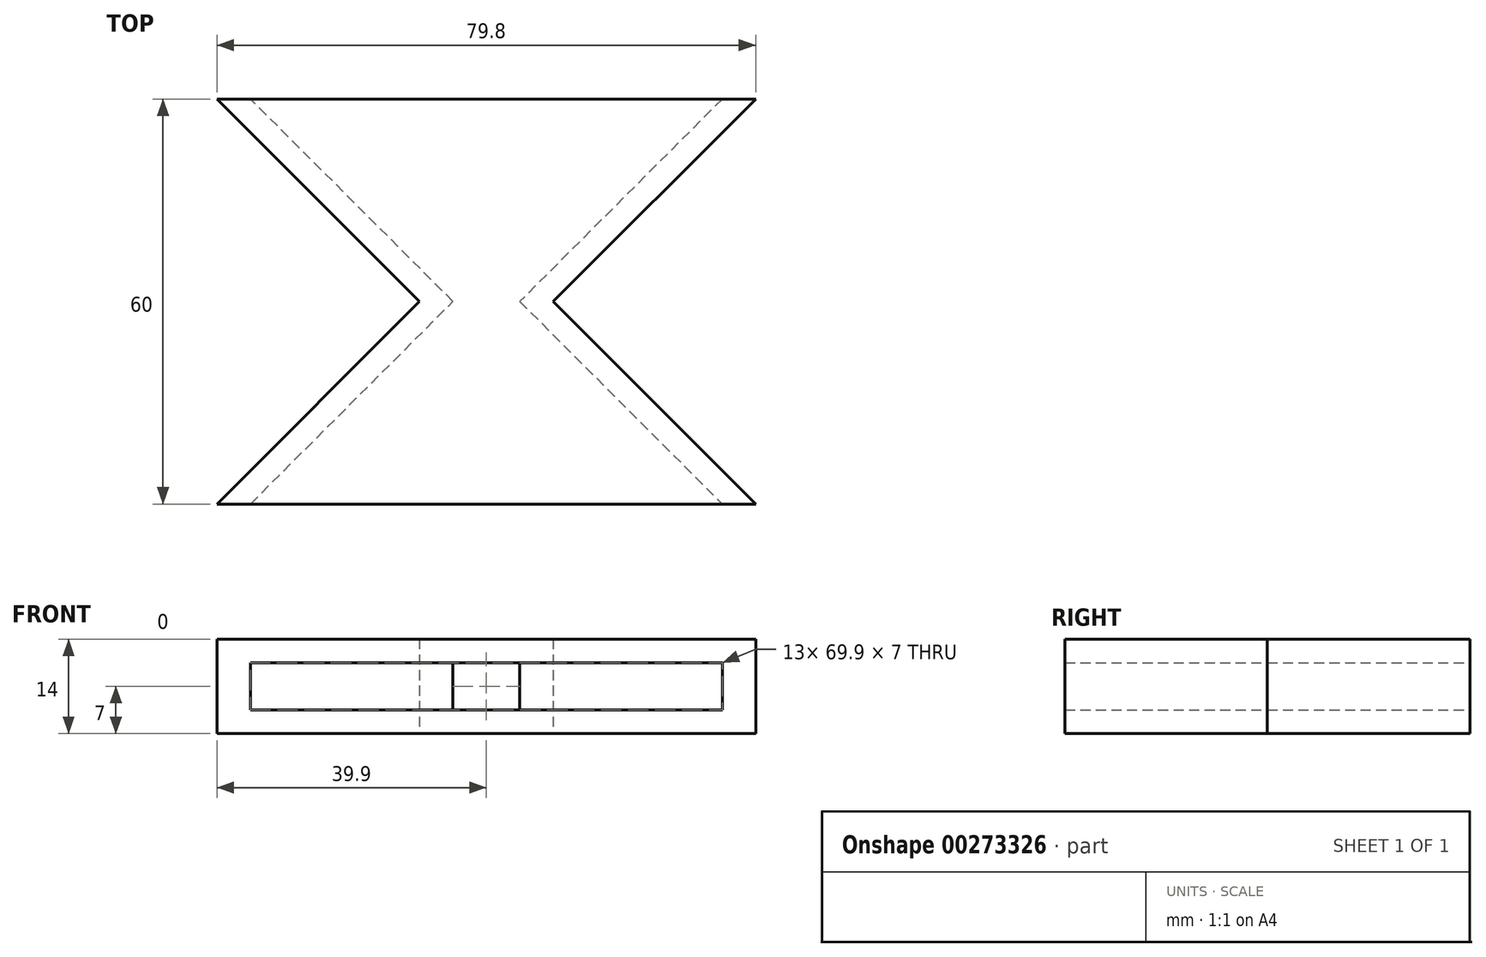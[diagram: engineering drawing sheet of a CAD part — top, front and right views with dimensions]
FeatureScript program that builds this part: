
annotation { "Feature Type Name" : "Feature", "Feature Type Description" : "" }
export const myFeature = defineFeature(function(context is Context, id is Id, definition is map)
    precondition{}
    {
        {
            var Q0;
            Q0=qCreatedBy(makeId("Top.planeOp"),FACE);
            var sketch = newSketch(context, id + "F0", { "sketchPlane" : qUnion([Q0])});
            skLineSegment(sketch, "E0", {"start": v(-39.9, 30) * mm, "end": v(39.9, 30) * mm});
            skLineSegment(sketch, "E1", {"start": v(39.9, 30) * mm, "end": v(9.9, 0) * mm});
            skLineSegment(sketch, "E2", {"start": v(9.9, 0) * mm, "end": v(39.9, -30) * mm});
            skLineSegment(sketch, "E3", {"start": v(39.9, -30) * mm, "end": v(-39.9, -30) * mm});
            skLineSegment(sketch, "E4", {"start": v(-39.9, -30) * mm, "end": v(-9.9, 0) * mm});
            skLineSegment(sketch, "E5", {"start": v(-9.9, 0) * mm, "end": v(-39.9, 30) * mm});
            skSolve(sketch);
        }
        {
            var Q0;
            Q0=makeQuery(id+"F0.imprint","IMPRINT",FACE,{"disambiguationData":[TD([[makeQuery(id+"F0.imprint","IMPRINT",EDGE,{"derivedFrom":sQuery(id+"F0.wireOp",EDGE,"E0")}),-1.0]])]});
            extrude(context, id + "F1", {"entities" : qUnion([Q0]), "depth" : 14 * mm});
        }
        {
            var Q0;
            Q0=makeQuery(id+"F1.opExtrude","SWEPT_FACE",FACE,{"disambiguationData":[OSD([sQuery(id+"F0.wireOp",EDGE,"E3")])]});
            var Q1;
            Q1=makeQuery(id+"F1.opExtrude","SWEPT_FACE",FACE,{"disambiguationData":[OSD([sQuery(id+"F0.wireOp",EDGE,"E0")])]});
            shell(context, id + "F2", {"entities" : qUnion([Q0, Q1]), "thickness" : 3.5 * mm});
        }
    });
